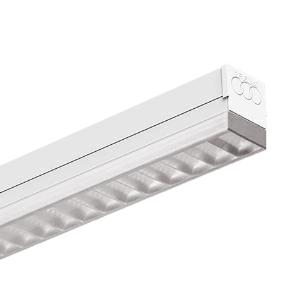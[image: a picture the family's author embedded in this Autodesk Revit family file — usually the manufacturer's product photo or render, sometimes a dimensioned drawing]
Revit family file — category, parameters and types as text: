
# Revit family: 3f_filippi_-_3f_zeta_dr_ugr_3f_filippi_-_10999_-_3f_zeta_dr_ugr_2x22_led_dali_l1783
name_source: partatom
category: Lighting Fixtures
units: mm (PartAtom-declared; Revit-internal decimal feet)

## family parameters
Cut with Voids When Loaded = No
Host = Face
Light Source = No
Part Type = Normal
Room Calculation Point = No
Round Connector Dimension = Use Diameter
Shared = No

## types (1)
- 3F Filippi - 3F Zeta DR UGR (1 x LED, 5361 lm, 49 W, 4000 K)
    Apparent Load = 49 VA
    Approval mark = CE
    CIE Flux Codes = 71 97 100 99 100
    Color Rendering = 80
    Color Temperature = 4000 K
    Control Gear = Electronic transformer
    Default Elevation = 1800 mm
    Description = ILLUMINOTECHNICAL
Luminous efficiency 100% (DLOR 99%, ULOR 1%).
Initial luminous flux of the luminaire 5361 lm.
Controlled direct symmetric distribution.
Installation Interdistance Transv.D = 1.30 x hu - Long.D = 1.20 x hu.
Average luminance <3000 cd/m² for radial angles >65°.
Tabular UGR (CIE 117 - 4H-8H; S=0.25H; 70/50/20): RUG 17.8 - 19.
Beam angle: 87° - 90°.
Luminous efficacy 109 lm/W.
Lifetime (L93/B10): 30000 h. (tq+25°C)
Lifetime (L90/B10): 50000 h. (tq+25°C)
Lifetime (L85/B10): 80000 h. (tq+25°C)
Lifetime (L80/B10): 100000 h. (tq+25°C)
Sudden decreased luminous flux after 50000 hours: 0% (C0).
Photobiological safety in compliance with IEC/TR 62778: RG0 risk exempt, (IEC 62471).
In compliance with IEC/EN 62722-2-1 - IEC/EN 62717 standards.

SOURCE
2 linear LED modules 22W/840.
Energy efficiency class (UE 2019/2020 - UE 2019/2015): D.
CIE 13.3 Colour rendering index: CRI >80 (R9 <50%).
IES TM-30 Fidelity Index: Rf = 84 Rg = 95.
CCT nominal colour temperature 4000 K.
Colour initial tolerance (MacAdam): SDCM 3.

MECHANICAL
Housing in hot-galvanised steel, painted in white polyester, obtained through rolling process.
Light unit in hot-galvanised steel, painted in white polyester base with fixing springs and retractable safety hooks in stainless steel.
Semi-specular aluminium internal louvre with prismatic methacrylate (PMMA) filter above the louvre blades for complete shielding of the louvre compartment.
Rectangular screen in self-extinguishing polycarbonate, UV stabilised, transparent, with smooth outer surface.
End caps in white polycarbonate.
Pair of stainless steel sliding brackets with sliding block screws.
Luminaire with limited surface temperature. - D - (EN 60598-2-24)
Dimensions: 1783x62 mm, height 81 mm. Weight 4.632 kg.
IP40 protection degree.
Mechanical strength to impacts IK06 (1 joule).
Glow-wire test resistance 850°C.

ELECTRICAL
Halogen Free DALI-2 DATI (Parts 251, 252, 253), PUSH-DIM, electronic wiring 230V-50/60Hz, power factor 0.95 at full load, THD <25%, constant output current, SELV, class I, 1 driver, 1 DALI addresse.
Power of the luminaire 49 W.
ENEC - CE.
SAFE FLICKER: PstLM=<1 and SVM=<0.4 (IEC TR 61547-1 and IEC TR 63158), to ensure a more comfortable and safe light.
Luminaire compliant with EN 60598-2-22 for power supply from a centralised emergency system CPSS (Central Power Supply System), not incorporated in the luminaire - high risk areas excluded. The default power and flux are 100% in AC and 15% in DC.
Ambient temperature from 0°C to +25°C.
Temperature class T6 max 85°C.
Relative humidity UR: <85%.

INSTALLATION
Ceiling / Suspended / Wall.
All accessories dedicated to this product are available on the Catalog and on our website www.3F-Filippi.com.

APPLICATIONS
Suitable product for food production plants (HACCP), IFS (Food Version 6), BRC (GSFS Food Version 7).
In environments with VDTs, managerial offices and staterooms, public offices and schools.

LIGHT MANAGEMENT
Recommended minimum setting: 10%.
The luminaire, equipped with (DALI-2 DATI) driver, can be controlled manually with 3F Easy Dim technology or automatically/manually with wired or wireless DALI/D2D control systems.
The D2D driver guarantees interoperability with other devices with the same certification by making the following information available:
Device Data (Part 251), Energy Report (Part 252), Diagnosis & Maintenance (Part 253).
In electrical systems without a regulation system (manual or automatic) and DALI bus, a suitable jumper must be made on the DA-DA terminals of the appliance.

WARNING
Luminaire designed for disposal/recycling at end-of-life.
Replaceable (LED only) light source by a professional. Replaceable control gear by a professional.
    Height = 81 mm
    Lamp = 1 x LED
    Lamp Light Flux = 5361 lm
    Lamp Power = 49 W
    Lamp count = 1
    Length = 1783 mm
    Lifetime = 50000 h
    Luminous efficacy = 109 lm/W
    Manufacturer = 3F Filippi
    ModVariant = No
    Model = 3F Filippi - 10999 - 3F Zeta DR UGR 2x22 LED DALI L1783
    Mounting Place = Ceiling
    Mounting Type = Surface mounted
    Number of Poles = 1
    OnlyDefault = Yes
    Power Factor = 1
    Product Name = 3F Filippi - 3F Zeta DR UGR
    Product group = ceiling mounted luminaire
    ProductGroupID = 3
    Protection Class = Protection class I
    Protection Degree = IP 40
    RLX_Detail_Level = 1
    RLX_Emergency_Light_Flux = 0 lm
    RLX_Emergency_Type = 0
    RLX_Emergency_Type_DB = No
    RlxData = <blob elided: 50121 chars, md5=e13d7815>
    Socket = socket
    Standby Power = 0 W
    System Light Flux = 5361 lm
    System Power = 49 W
    Type Comments = Product without accessories
    Type Image = 3ffilippi_3f_zeta_dr_ugr.jpg
    URL = http://relux.com
    VarID = ---
    Voltage = 0 V
    Weight = 0.00 kg
    Width = 62 mm  [stored 0.203412 ft]

note: [stored X ft] marks values corroborated as IEEE doubles in the binary element streams (Revit-internal decimal feet)

## geometry (parser evidence)
native form markers: Blend x4, Sweep x11
no freeform markers — native parametric forms only
